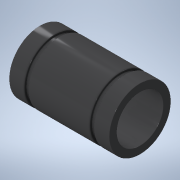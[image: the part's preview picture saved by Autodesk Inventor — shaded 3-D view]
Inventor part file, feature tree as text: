
AUTODESK INVENTOR PART (.ipt)
format: ipt  version: 2020.2 (Build 242310000, 310)  size: 195,072 bytes
history: native  units: mm
features: sketch x2, other x1, extrude x1, revolve x1, fillet x1, projected_geometry x1
ambient origin geometry x8: Origin, YZ Plane, XZ Plane, XY Plane, X Axis, Y Axis, Z Axis, Center Point
bodies: Body1 (feature_tree)
feature tree (7):
  other  "Bryła1"
  extrude  "Wyciągnięcie proste1"  Depth=16.0mm
  revolve  "Obrót1"
  fillet  "Zaokrąglenie1"  Radius=12.0mm
  sketch  "Szkic1"
  sketch  "Szkic2"
  projected_geometry  "Pętla rzutowana1"
